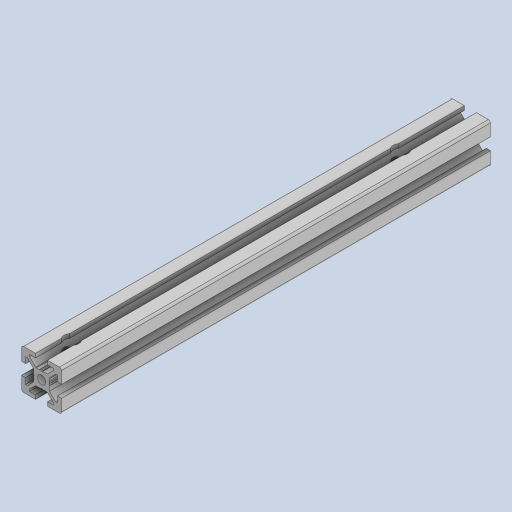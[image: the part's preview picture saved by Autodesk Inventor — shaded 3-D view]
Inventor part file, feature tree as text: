
AUTODESK INVENTOR PART (.ipt)
format: ipt  version: 2023 (Build 270158000, 158)  size: 326,144 bytes
history: native  units: mm
features: other x7, sketch x4, revolve x2, extrude x1, hole x1
ambient origin geometry x8: Origin, YZ Plane, XZ Plane, XY Plane, X Axis, Y Axis, Z Axis, Center Point
bodies: Solid1 (feature_tree)
feature tree (15):
  extrude  "Extrusion1"  TaperAngle=360.0deg  [1 undecoded]
  hole  "Hole1"  [1 undecoded]
  revolve  "Revolution1"  [1 undecoded]
  revolve  "Revolution2"  [1 undecoded]
  other  "C1_XY"
  other  "C1_YZ"
  other  "C1_ZX"
  other  "C1_X"
  other  "C1_Y"
  other  "C1_Z"
  other  "C1_Center"
  sketch  "Sketch_75"
  sketch  "Sketch2"  dims[d0=215.0mm d1=0.0mm]
  sketch  "Sketch_29"  dims[d2=4.2mm d3=6.0mm d4=4.0mm d5=2.0mm d6=90.0deg d7=215.0mm d8=0.0mm d9=360.0deg]
  sketch  "Sketch_32"  dims[d10=360.0deg d11=0.0mm]
note: 4 required parameter values undecoded (feature->parameter linkage not recoverable at this tier; creation-order binding heuristic only, values carry confidence <= 0.55)
